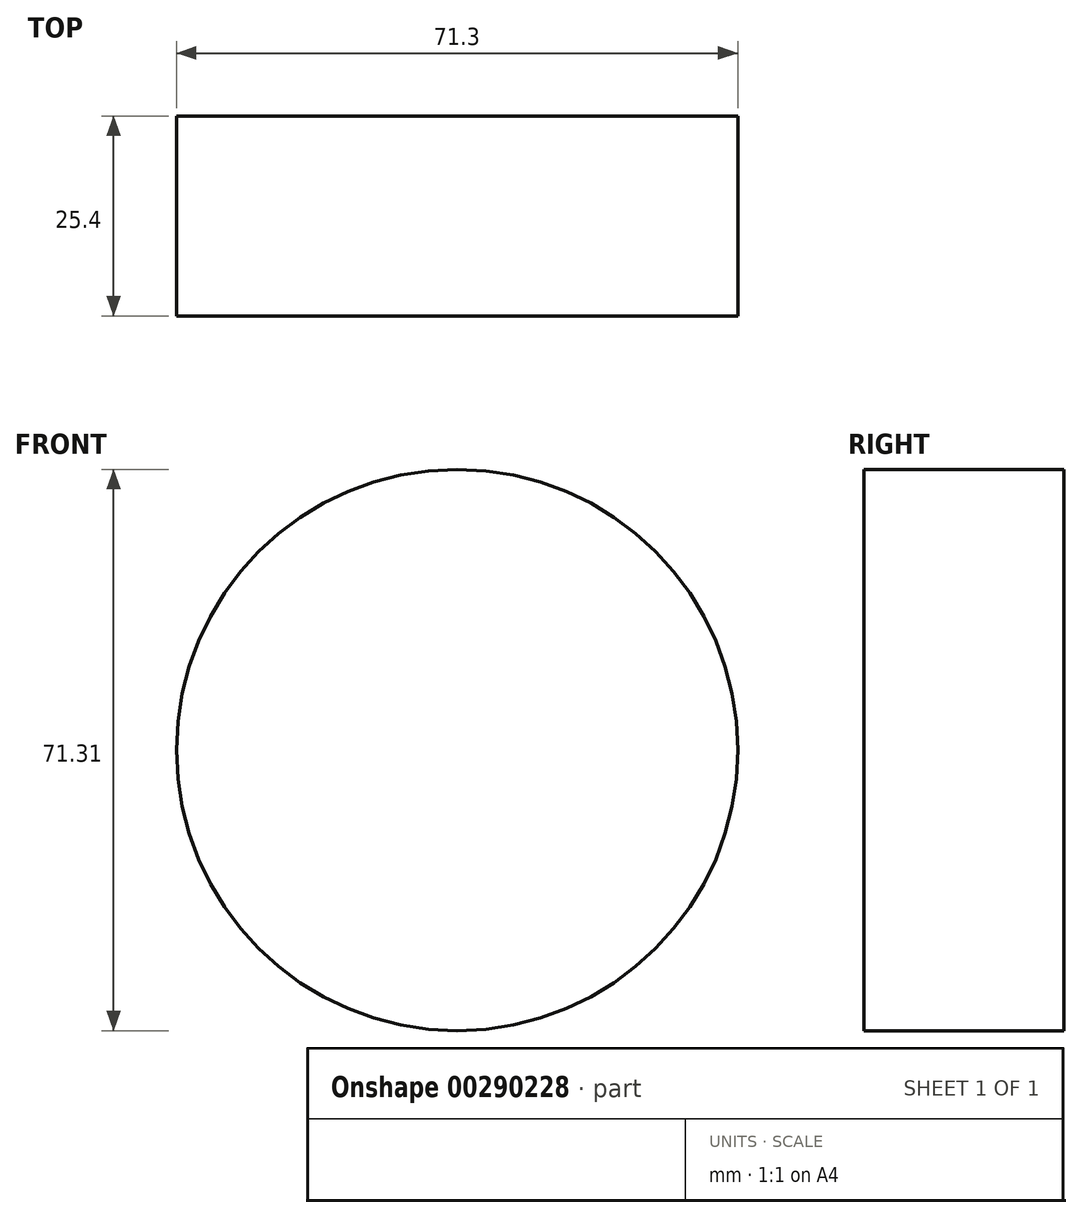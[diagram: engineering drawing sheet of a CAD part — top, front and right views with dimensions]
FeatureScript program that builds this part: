
annotation { "Feature Type Name" : "Feature", "Feature Type Description" : "" }
export const myFeature = defineFeature(function(context is Context, id is Id, definition is map)
    precondition{}
    {
        {
            var Q0;
            Q0=qCreatedBy(makeId("Front.planeOp"),FACE);
            var sketch = newSketch(context, id + "F0", { "sketchPlane" : qUnion([Q0])});
            skCircle(sketch, "E0", {"center": v(-13.8, 20.02) * mm, "radius": 35.65 * mm});
            skSolve(sketch);
        }
        {
            var Q0;
            Q0 = qSketchRegion(id + "F0", true);
            extrude(context, id + "F1", {"entities" : qUnion([Q0]), "depth" : 25.4 * mm});
        }
    });
